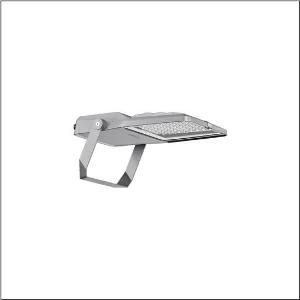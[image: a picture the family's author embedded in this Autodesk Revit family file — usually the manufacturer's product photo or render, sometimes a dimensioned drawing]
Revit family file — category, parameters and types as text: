
# Revit family: floodlight_fl_21_mini___pl61_5xa7773c4c1a_fa47
name_source: partatom
category: Lighting Fixtures
units: mm (PartAtom-declared; Revit-internal decimal feet)

## family parameters
Cut with Voids When Loaded = No
Host = Face
Light Source = No
Part Type = Normal
Room Calculation Point = No
Round Connector Dimension = Use Diameter
Shared = No

## types (1)
- --- (1 x LED, 19990 lm, 163.5 W, 4000K)
    Apparent Load = 163 VA
    CIE Flux Codes = 33 65 98 100 100
    Color Rendering = 70
    Color Temperature = 4000K
    Default Elevation = 1800 mm
    Description = Floodlight FL 21 mini, floodlight, primary light control with lens, of PMMA, primary optical cover: protective disc, of toughened safety glass, transparent, light distribution: PL61, light emission: direct distribution, installation type: surface-mounted, LED, High Power LED, rated luminous flux: 19.990lm, luminous efficacy: 122lm/W, light colour: 740, colour temperature: 4000K, control: Temp-Guard, with terminal, 6-pole, mains connection: 220..240V, AC, 50/60Hz, start of lifetime: 164W, luminaire housing, of diecast aluminium, powder-coated, Siteco® metallic grey (DB 702S), corrosivity category C5 mid according to DIN EN ISO 12944, sealing non-destructively replaceable, mounting bracket, of steel, galvanised, powder-coated, Siteco® metallic grey (DB 702S), ON/OFF, protection rating (complete): IP66, insulation class (complete): insulation class I (protective earthing), certification: CE, ENEC, VDE, protection symbol: D, impact resistance: IK08, permissible operating ambient temperature: -40..+40°C, permissible operating ambient temperature for outdoor applications: -40..+50°C, standard: DIN EN 12944, LABS conformity tested according to VDMA 24364:2018-05, packaging unit: 1 piece

Light Distribution: PL61
    Height = 70 mm
    Lamp = 1 x LED
    Lamp Light Flux = 19990 lm
    Lamp Power = 163.5 W
    Lamp count = 1
    Length = 485 mm
    Luminous efficacy = 122 lm/W
    Manufacturer = Siteco
    ModVariant = No
    Model = 5XA7773C4C1A
    Number of Poles = 1
    OnlyDefault = Yes
    Power Factor = 1
    Product Name = Floodlight FL 21 mini | PL61
    Product group = floodlight | pylon annexe
    ProductGroupID = 6200
    Protection Class = Protection class I
    Protection Degree = IP 66
    RLX_Detail_Level = 1
    RLX_Emergency_Light_Flux = 0 lm
    RLX_Emergency_Type = 0
    RLX_Emergency_Type_DB = No
    RlxData = <blob elided: 94253 chars, md5=2e0f25e8>
    Socket = socket
    Standby Power = 0 W
    System Light Flux = 19990 lm
    System Power = 163 W
    Type Comments = factory setting: luminous flux: 100 % | (ON | - | - | - | - | - | - | -) | 825 mA
    Type Image = l_1006845.jpg
    URL = http://relux.com
    VarID = @adj_123759
    Voltage = 0 V
    Weight = 0.00 kg
    Width = 337 mm

## geometry (parser evidence)
native form markers: Blend x4, Sweep x13
no freeform markers — native parametric forms only
